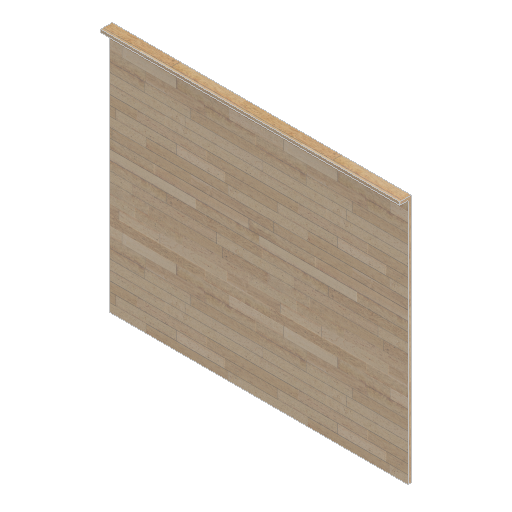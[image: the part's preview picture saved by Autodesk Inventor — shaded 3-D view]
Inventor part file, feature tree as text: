
AUTODESK INVENTOR PART (.ipt)
format: ipt  version: 2025.1 (Build 291241000, 241)  size: 405,504 bytes
history: native  units: mm
features: extrude x2, other x1
ambient origin geometry x8: Origin, YZ Plane, XZ Plane, XY Plane, X Axis, Y Axis, Z Axis, Center Point
bodies: Body1 (feature_tree)
feature tree (3):
  other  "Bryła1"
  extrude  "Wyciągnięcie proste1"  Depth=1800.0mm
  extrude  "Wyciągnięcie proste2"  Depth=1500.0mm
